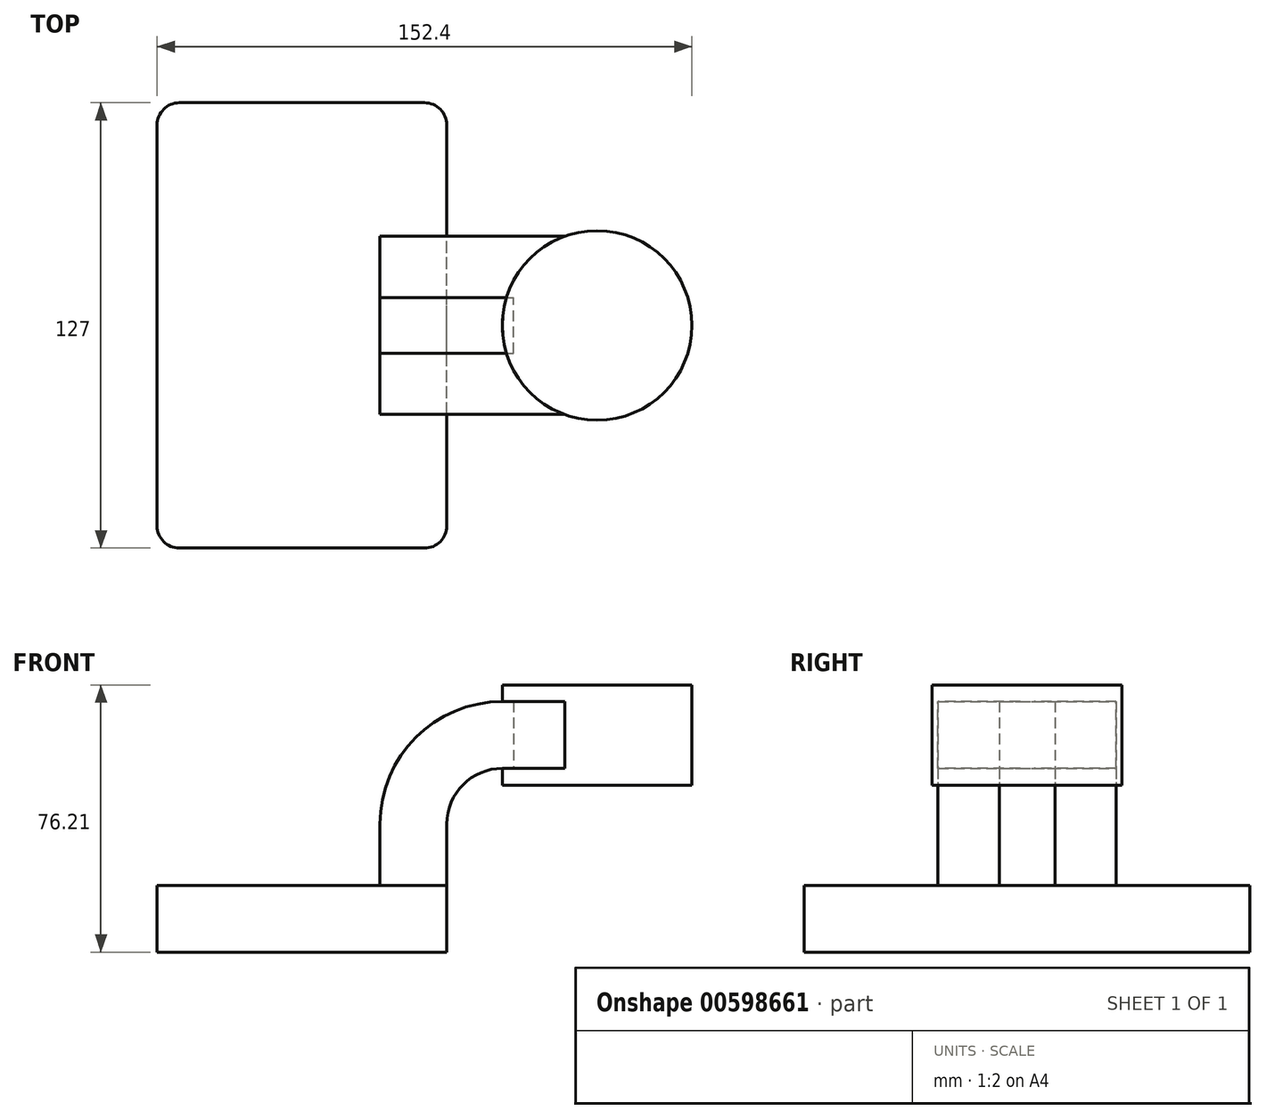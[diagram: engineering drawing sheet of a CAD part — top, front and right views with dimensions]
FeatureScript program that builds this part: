
annotation { "Feature Type Name" : "Feature", "Feature Type Description" : "" }
export const myFeature = defineFeature(function(context is Context, id is Id, definition is map)
    precondition{}
    {
        {
            var Q0;
            Q0=qCreatedBy(makeId("Front.planeOp"),FACE);
            var sketch = newSketch(context, id + "F0", { "sketchPlane" : qUnion([Q0])});
            skLineSegment(sketch, "E0.bottom", {"start": v(-41.28, 9.52) * mm, "end": v(41.27, 9.53) * mm});
            skLineSegment(sketch, "E0.top", {"start": v(-41.27, -9.53) * mm, "end": v(41.28, -9.53) * mm});
            skLineSegment(sketch, "E0.left", {"start": v(-41.28, 9.52) * mm, "end": v(-41.27, -9.53) * mm});
            skLineSegment(sketch, "E0.right", {"start": v(41.28, 9.53) * mm, "end": v(41.28, -9.52) * mm});
            skPoint(sketch, "E0.middle", {"position": v(0, 0) * mm});
            skLineSegment(sketch, "E1.bottom", {"start": v(60.32, 66.68) * mm, "end": v(111.12, 66.68) * mm});
            skLineSegment(sketch, "E1.top", {"start": v(60.32, 38.1) * mm, "end": v(111.13, 38.1) * mm});
            skLineSegment(sketch, "E1.left", {"start": v(60.32, 66.68) * mm, "end": v(60.32, 38.1) * mm});
            skLineSegment(sketch, "E1.right", {"start": v(111.12, 66.68) * mm, "end": v(111.12, 38.1) * mm});
            skPoint(sketch, "E1.middle", {"position": v(85.72, 52.39) * mm});
            skLineSegment(sketch, "E2", {"start": v(41.27, 9.53) * mm, "end": v(41.27, 27) * mm});
            skArc(sketch, "E3", {"start": v(41.27, 27) * mm, "mid": v(45.92, 38.23) * mm, "end": v(57.15, 42.88) * mm});
            skLineSegment(sketch, "E4", {"start": v(57.15, 42.88) * mm, "end": v(84.1, 42.88) * mm});
            skLineSegment(sketch, "E5.0", {"start": v(57.15, 61.93) * mm, "end": v(84.1, 61.93) * mm});
            skArc(sketch, "E5.1", {"start": v(22.22, 27) * mm, "mid": v(32.45, 51.7) * mm, "end": v(57.15, 61.93) * mm});
            skLineSegment(sketch, "E5.2", {"start": v(22.22, 9.53) * mm, "end": v(22.22, 27) * mm});
            skLineSegment(sketch, "E6", {"start": v(84.1, 66.68) * mm, "end": v(84.1, 38.1) * mm});
            skFitSpline(sketch, "E7", {"points": [v(-41.28, 9.52) * mm, v(60.32, 61.93) * mm], "startDerivative": vector(4.31, 126.92) * mm, "endDerivative": vector(139.42, -43.4) * mm});
            skSolve(sketch);
        }
        {
            var Q0;
            Q0=makeQuery(id+"F0.imprint","IMPRINT",FACE,{"disambiguationData":[TD([[makeQuery(id+"F0.imprint","IMPRINT",EDGE,{"derivedFrom":sQuery(id+"F0.wireOp",EDGE,"E0.top")}),1.0]])]});
            extrude(context, id + "F1", {"entities" : qUnion([Q0]), "endBound" : BoundingType.SYMMETRIC, "depth" : 127 * mm, "offsetDistance" : 25.4 * mm});
        }
        {
            var Q0;
            {var subQ1=sQuery(id+"F0.wireOp",EDGE,"E2");Q0=makeQuery(id+"F0.imprint","IMPRINT",FACE,{"disambiguationData":[TD([[makeQuery(id+"F0.imprint","IMPRINT",EDGE,{"derivedFrom":subQ1}),1.0]])]});}
            extrude(context, id + "F2", {"entities" : qUnion([Q0]), "endBound" : BoundingType.SYMMETRIC, "depth" : 50.8 * mm, "offsetDistance" : 25.4 * mm});
        }
        {
            var Q0;
            {var subQ3=sQuery(id+"F0.wireOp",EDGE,"E4");var subQ5=sQuery(id+"F0.wireOp",EDGE,"E6");var subQ6=makeQuery(id+"F0.imprint","INTERSECT",VERTEX,{"derivedFrom":[subQ3,subQ5]});Q0=makeQuery(id+"F0.imprint","IMPRINT",FACE,{"disambiguationData":[TD([[makeQuery(id+"F0.imprint","IMPRINT",EDGE,{"disambiguationData":[TD([[subQ6,1.0]])],"derivedFrom":subQ3}),1.0]])]});}
            extrude(context, id + "F3", {"entities" : qUnion([Q0]), "operationType" : NewBodyOperationType.ADD, "endBound" : BoundingType.SYMMETRIC, "depth" : 50.8 * mm, "offsetDistance" : 25.4 * mm});
        }
        {
            var Q0;
            {var subQ0=sQuery(id+"F0.wireOp",EDGE,"E1.right");Q0=makeQuery(id+"F0.imprint","IMPRINT",FACE,{"disambiguationData":[TD([[makeQuery(id+"F0.imprint","IMPRINT",EDGE,{"derivedFrom":subQ0}),-1.0]])]});}
            var Q1;
            Q1=sQuery(id+"F0.wireOp",EDGE,"E6");
            revolve(context, id + "F4", {"operationType" : NewBodyOperationType.ADD, "entities" : qUnion([Q0]), "axis" : qUnion([Q1]), "revolveType" : RevolveType.FULL});
        }
        {
            var Q0;
            {var subQ0=sQuery(id+"F0.wireOp",EDGE,"E5.1");Q0=makeQuery(id+"F0.imprint","IMPRINT",FACE,{"disambiguationData":[TD([[makeQuery(id+"F0.imprint","IMPRINT",EDGE,{"derivedFrom":subQ0}),1.0]])]});}
            extrude(context, id + "F5", {"entities" : qUnion([Q0]), "endBound" : BoundingType.SYMMETRIC, "depth" : 15.88 * mm, "offsetDistance" : 25.4 * mm});
        }
        {
            var Q0;
            Q0=makeQuery(id+"F1.opExtrude","CAP_EDGE",EDGE,{"disambiguationData":[OSD([sQuery(id+"F0.wireOp",EDGE,"E0.right")])],"isStart":false});
            var Q1;
            Q1=makeQuery(id+"F1.opExtrude","CAP_EDGE",EDGE,{"disambiguationData":[OSD([sQuery(id+"F0.wireOp",EDGE,"E0.left")])],"isStart":false});
            var Q2;
            Q2=makeQuery(id+"F1.opExtrude","CAP_EDGE",EDGE,{"disambiguationData":[OSD([sQuery(id+"F0.wireOp",EDGE,"E0.left")])],"isStart":true});
            var Q3;
            Q3=makeQuery(id+"F1.opExtrude","CAP_EDGE",EDGE,{"disambiguationData":[OSD([sQuery(id+"F0.wireOp",EDGE,"E0.right")])],"isStart":true});
            fillet(context, id + "F6", {"entities" : qUnion([Q0, Q1, Q2, Q3]), "radius" : 6.35 * mm, "tangentPropagation" : true, "allowEdgeOverflow" : false});
        }
    });
